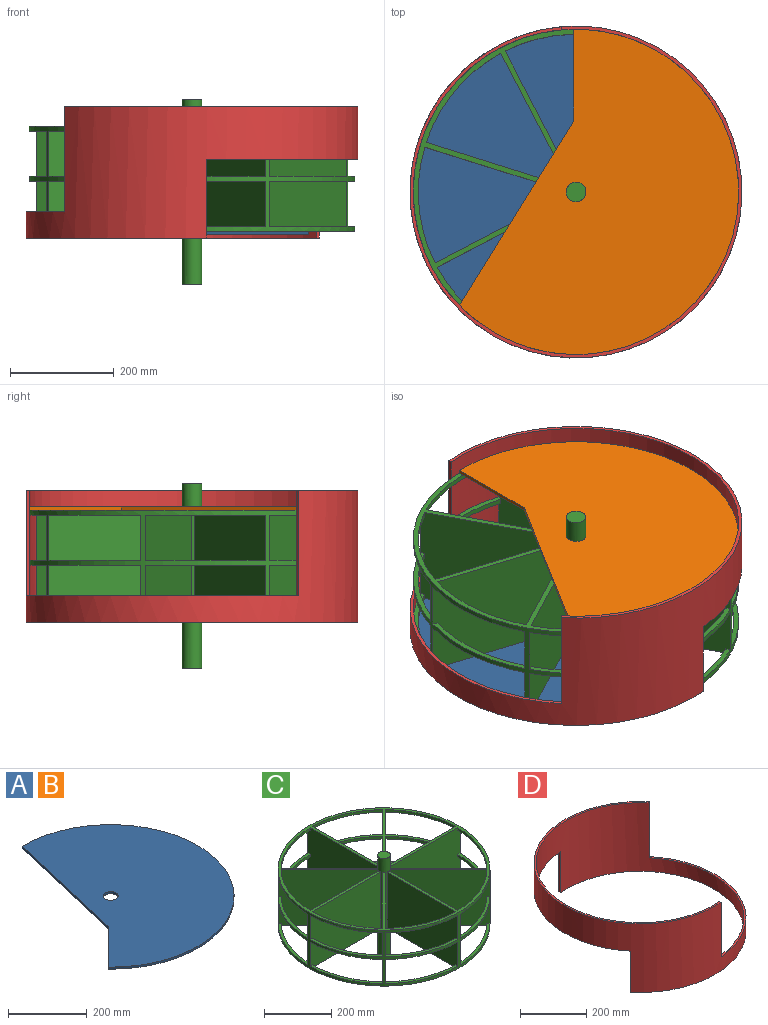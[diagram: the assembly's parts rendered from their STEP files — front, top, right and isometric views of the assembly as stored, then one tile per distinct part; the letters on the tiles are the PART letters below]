
ASSEMBLY  parts=4 mates=3
PART A: 6 faces, bbox 539.9x628.7x6.4 mm
  f0: plane 407.64x95.32mm, normal (-0.97,0.23,0), area 2658.3mm2, adj f1,f3,f4,f5
  f1: plane 125.52x125.52mm, normal (-0.71,0.71,0), area 1127.2mm2, adj f0,f3,f4,f5
  f2: cylinder r=19.05mm len=38.1mm, axis (0,0,-1), area 760.1mm2, adj f4,f5
  f3: cylinder r=314.33mm len=628.65mm, axis (0,0,-1), area 7898.6mm2, adj f0,f1,f4,f5
  f4: plane 628.65x539.93mm, normal (0,0,1), area 210723.4mm2, adj f0,f1,f2,f3
  f5: plane 628.65x539.93mm, normal (0,0,-1), area 210723.4mm2, adj f0,f1,f2,f3
PART B: same geometry as A
PART C: 78 faces, bbox 628.7x628.7x355.6 mm
  f0: plane 214.11x95.42mm, normal (0,0,1), area 2225.1mm2, adj f1,f53,f54,f76
  f1: cylinder r=304.8mm len=207.37mm, axis (0,0,-1), area 2189.5mm2, adj f0,f54,f56,f76
  f2: cylinder r=304.8mm len=207.37mm, axis (0,0,-1), area 2189.5mm2, adj f3,f4,f54,f76
  f3: plane 214.11x95.42mm, normal (0,0,1), area 2225.1mm2, adj f2,f53,f54,f76
  f4: plane 214.11x95.42mm, normal (0,0,-1), area 2225.1mm2, adj f2,f53,f54,f76
  f5: plane 214.11x95.42mm, normal (0,0,-1), area 2225.1mm2, adj f6,f53,f54,f76
  f6: cylinder r=304.8mm len=207.37mm, axis (0,0,-1), area 2189.5mm2, adj f5,f54,f55,f76
  f7: plane 214.11x95.42mm, normal (0,0,1), area 2225.1mm2, adj f8,f53,f74,f77
  f8: cylinder r=304.8mm len=207.37mm, axis (0,0,-1), area 2189.5mm2, adj f7,f56,f74,f77
  f9: cylinder r=304.8mm len=207.37mm, axis (0,0,-1), area 2189.5mm2, adj f10,f11,f74,f77
  f10: plane 214.11x95.42mm, normal (0,0,1), area 2225.1mm2, adj f9,f53,f74,f77
  f11: plane 214.11x95.42mm, normal (0,0,-1), area 2225.1mm2, adj f9,f53,f74,f77
  f12: plane 214.11x95.42mm, normal (0,0,-1), area 2225.1mm2, adj f13,f53,f74,f77
  f13: cylinder r=304.8mm len=207.37mm, axis (0,0,-1), area 2189.5mm2, adj f12,f55,f74,f77
  f14: plane 214.11x95.42mm, normal (0,0,1), area 2225.1mm2, adj f15,f53,f72,f75
  f15: cylinder r=304.8mm len=207.37mm, axis (0,0,-1), area 2189.5mm2, adj f14,f56,f72,f75
  f16: cylinder r=304.8mm len=207.37mm, axis (0,0,-1), area 2189.5mm2, adj f17,f18,f72,f75
  f17: plane 214.11x95.42mm, normal (0,0,1), area 2225.1mm2, adj f16,f53,f72,f75
  f18: plane 214.11x95.42mm, normal (0,0,-1), area 2225.1mm2, adj f16,f53,f72,f75
  f19: plane 214.11x95.42mm, normal (0,0,-1), area 2225.1mm2, adj f20,f53,f72,f75
  f20: cylinder r=304.8mm len=207.37mm, axis (0,0,-1), area 2189.5mm2, adj f19,f55,f72,f75
  f21: plane 214.11x95.42mm, normal (0,0,1), area 2225.1mm2, adj f22,f53,f70,f73
  f22: cylinder r=304.8mm len=207.37mm, axis (0,0,-1), area 2189.5mm2, adj f21,f56,f70,f73
  f23: cylinder r=304.8mm len=207.37mm, axis (0,0,-1), area 2189.5mm2, adj f24,f25,f70,f73
  f24: plane 214.11x95.42mm, normal (0,0,1), area 2225.1mm2, adj f23,f53,f70,f73
  f25: plane 214.11x95.42mm, normal (0,0,-1), area 2225.1mm2, adj f23,f53,f70,f73
  f26: plane 214.11x95.42mm, normal (0,0,-1), area 2225.1mm2, adj f27,f53,f70,f73
  f27: cylinder r=304.8mm len=207.37mm, axis (0,0,-1), area 2189.5mm2, adj f26,f55,f70,f73
  f28: plane 214.11x95.42mm, normal (0,0,1), area 2225.1mm2, adj f29,f53,f68,f71
  f29: cylinder r=304.8mm len=207.37mm, axis (0,0,-1), area 2189.5mm2, adj f28,f56,f68,f71
  f30: cylinder r=304.8mm len=207.37mm, axis (0,0,-1), area 2189.5mm2, adj f31,f32,f68,f71
  f31: plane 214.11x95.42mm, normal (0,0,1), area 2225.1mm2, adj f30,f53,f68,f71
  f32: plane 214.11x95.42mm, normal (0,0,-1), area 2225.1mm2, adj f30,f53,f68,f71
  f33: plane 214.11x95.42mm, normal (0,0,-1), area 2225.1mm2, adj f34,f53,f68,f71
  f34: cylinder r=304.8mm len=207.37mm, axis (0,0,-1), area 2189.5mm2, adj f33,f55,f68,f71
  f35: plane 214.11x95.42mm, normal (0,0,1), area 2225.1mm2, adj f36,f53,f66,f69
  f36: cylinder r=304.8mm len=207.37mm, axis (0,0,-1), area 2189.5mm2, adj f35,f56,f66,f69
  f37: cylinder r=304.8mm len=207.37mm, axis (0,0,-1), area 2189.5mm2, adj f38,f39,f66,f69
  f38: plane 214.11x95.42mm, normal (0,0,1), area 2225.1mm2, adj f37,f53,f66,f69
  f39: plane 214.11x95.42mm, normal (0,0,-1), area 2225.1mm2, adj f37,f53,f66,f69
  f40: plane 214.11x95.42mm, normal (0,0,-1), area 2225.1mm2, adj f41,f53,f66,f69
  f41: cylinder r=304.8mm len=207.37mm, axis (0,0,-1), area 2189.5mm2, adj f40,f55,f66,f69
  f42: plane 214.11x95.42mm, normal (0,0,1), area 2225.1mm2, adj f43,f53,f64,f67
  f43: cylinder r=304.8mm len=207.37mm, axis (0,0,-1), area 2189.5mm2, adj f42,f56,f64,f67
  f44: cylinder r=304.8mm len=207.37mm, axis (0,0,-1), area 2189.5mm2, adj f45,f46,f64,f67
  f45: plane 214.11x95.42mm, normal (0,0,1), area 2225.1mm2, adj f44,f53,f64,f67
  f46: plane 214.11x95.42mm, normal (0,0,-1), area 2225.1mm2, adj f44,f53,f64,f67
  f47: plane 214.11x95.42mm, normal (0,0,-1), area 2225.1mm2, adj f48,f53,f64,f67
  f48: cylinder r=304.8mm len=207.37mm, axis (0,0,-1), area 2189.5mm2, adj f47,f55,f64,f67
  f49: cylinder r=19.05mm len=355.6mm, axis (0,0,-1), area 26913.6mm2, adj f50,f51,f52,f54,f55,f56,f64,f65
  f50: plane 38.1x38.1mm, normal (0,0,1), area 1140.1mm2, adj f49
  f51: plane 38.1x38.1mm, normal (0,0,-1), area 1140.1mm2, adj f49
  f52: plane 295.84x203.2mm, normal (1,0,0), area 59843.3mm2, adj f49,f53,f55,f56,f57,f58,f59,f60
  f53: cylinder r=314.33mm len=628.65mm, axis (0,0,-1), area 69741.5mm2, adj f0,f3,f4,f5,f7,f10,f11,f12
  f54: plane 295.84x203.2mm, normal (-1,0,0), area 59843.3mm2, adj f0,f1,f2,f3,f4,f5,f6,f49
  f55: plane 628.65x628.65mm, normal (0,0,1), area 40315mm2, adj f6,f13,f20,f27,f34,f41,f48,f49
  f56: plane 628.65x628.65mm, normal (0,0,-1), area 40315mm2, adj f1,f8,f15,f22,f29,f36,f43,f49
  f57: plane 214.11x95.42mm, normal (0,0,1), area 2225.1mm2, adj f52,f53,f58,f65
  f58: cylinder r=304.8mm len=207.37mm, axis (0,0,-1), area 2189.5mm2, adj f52,f56,f57,f65
  f59: cylinder r=304.8mm len=207.37mm, axis (0,0,-1), area 2189.5mm2, adj f52,f60,f61,f65
  f60: plane 214.11x95.42mm, normal (0,0,1), area 2225.1mm2, adj f52,f53,f59,f65
  f61: plane 214.11x95.42mm, normal (0,0,-1), area 2225.1mm2, adj f52,f53,f59,f65
  f62: plane 214.11x95.42mm, normal (0,0,-1), area 2225.1mm2, adj f52,f53,f63,f65
  f63: cylinder r=304.8mm len=207.37mm, axis (0,0,-1), area 2189.5mm2, adj f52,f55,f62,f65
  f64: plane 209.19x209.19mm, normal (0.71,-0.71,0), area 59843.3mm2, adj f42,f43,f44,f45,f46,f47,f48,f49
  f65: plane 209.19x209.19mm, normal (-0.71,0.71,0), area 59843.3mm2, adj f49,f53,f55,f56,f57,f58,f59,f60
  f66: plane 295.84x203.2mm, normal (0,-1,0), area 59843.3mm2, adj f35,f36,f37,f38,f39,f40,f41,f49
  f67: plane 295.84x203.2mm, normal (0,1,0), area 59843.3mm2, adj f42,f43,f44,f45,f46,f47,f48,f49
  f68: plane 209.19x209.19mm, normal (-0.71,-0.71,0), area 59843.3mm2, adj f28,f29,f30,f31,f32,f33,f34,f49
  f69: plane 209.19x209.19mm, normal (0.71,0.71,0), area 59843.3mm2, adj f35,f36,f37,f38,f39,f40,f41,f49
  f70: plane 295.84x203.2mm, normal (-1,0,0), area 59843.3mm2, adj f21,f22,f23,f24,f25,f26,f27,f49
  f71: plane 295.84x203.2mm, normal (1,0,0), area 59843.3mm2, adj f28,f29,f30,f31,f32,f33,f34,f49
  f72: plane 209.19x209.19mm, normal (-0.71,0.71,0), area 59843.3mm2, adj f14,f15,f16,f17,f18,f19,f20,f49
  f73: plane 209.19x209.19mm, normal (0.71,-0.71,0), area 59843.3mm2, adj f21,f22,f23,f24,f25,f26,f27,f49
  f74: plane 295.84x203.2mm, normal (0,1,0), area 59843.3mm2, adj f7,f8,f9,f10,f11,f12,f13,f49
  f75: plane 295.84x203.2mm, normal (0,-1,0), area 59843.3mm2, adj f14,f15,f16,f17,f18,f19,f20,f49
  f76: plane 209.19x209.19mm, normal (0.71,0.71,0), area 59843.3mm2, adj f0,f1,f2,f3,f4,f5,f6,f49
  f77: plane 209.19x209.19mm, normal (-0.71,-0.71,0), area 59843.3mm2, adj f7,f8,f9,f10,f11,f12,f13,f49
PART D: 10 faces, bbox 641.4x641.4x254 mm
  f0: cylinder r=314.33mm len=628.65mm, axis (0,0,-1), area 257787.4mm2, adj f1,f2,f4,f5,f6,f7,f8,f9
  f1: plane 641.35x566.33mm, normal (0,0,-1), area 8269.2mm2, adj f0,f3,f7,f8
  f2: plane 641.35x566.33mm, normal (0,0,1), area 8269.2mm2, adj f0,f3,f4,f5
  f3: cylinder r=320.68mm len=641.35mm, axis (0,0,-1), area 262995.3mm2, adj f1,f2,f4,f5,f6,f7,f8,f9
  f4: plane 203.2x4.86mm, normal (0.64,-0.77,0), area 1290.3mm2, adj f0,f2,f3,f6
  f5: plane 203.2x6.33mm, normal (1,0.09,0), area 1290.3mm2, adj f0,f2,f3,f6
  f6: plane 525.58x293.28mm, normal (0,0,1), area 4398.5mm2, adj f0,f3,f4,f5
  f7: plane 152.4x6.33mm, normal (-1,-0.09,0), area 967.7mm2, adj f0,f1,f3,f9
  f8: plane 152.4x4.86mm, normal (-0.64,0.77,0), area 967.7mm2, adj f0,f1,f3,f9
  f9: plane 525.58x293.28mm, normal (0,0,-1), area 4398.5mm2, adj f0,f3,f7,f8
PLACE A rot(axis=(0.38,0.92,0),180deg) t=(-215.53,215.53,-38.1)mm
PLACE B rot(axis=(0.92,-0.38,0),180deg) t=(215.53,-215.53,171.45)mm
PLACE C rot(axis=(0,0,-1),152.4deg) t=(-270.18,-141.09,-241.3)mm
PLACE D rot(axis=(0,0,-1),180deg) t=(-304.8,0,-457.2)mm
MATE fastened A.f2 <-> B.f2  axis (0,0,1) through (0,0,-241.3)mm
MATE revolute C.f1 <-> B.f2  axis (0,0,1) through (0,0,-38.1)mm
MATE revolute A.f2 <-> D.f0  axis (0,0,-1) through (0,0,-247.65)mm
